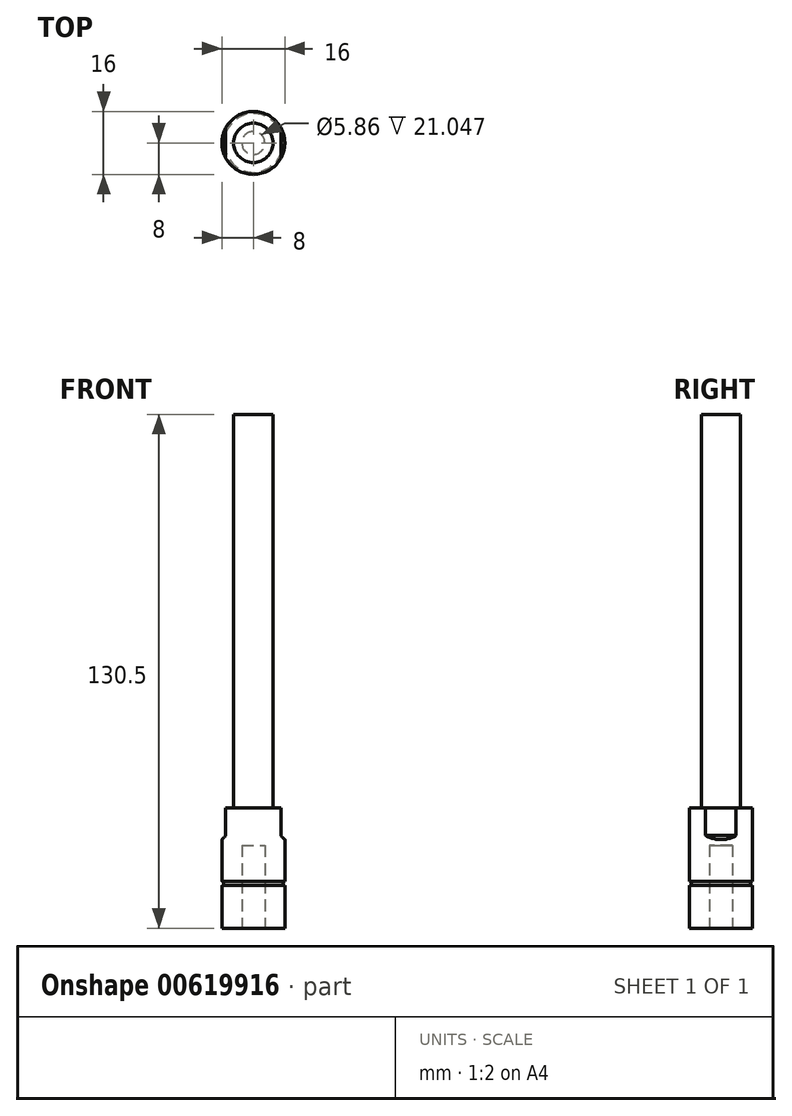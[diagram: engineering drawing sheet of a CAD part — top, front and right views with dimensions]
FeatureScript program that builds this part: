
annotation { "Feature Type Name" : "Feature", "Feature Type Description" : "" }
export const myFeature = defineFeature(function(context is Context, id is Id, definition is map)
    precondition{}
    {
        {
            var Q0;
            Q0=qCreatedBy(makeId("Front.planeOp"),FACE);
            var sketch = newSketch(context, id + "F0", { "sketchPlane" : qUnion([Q0])});
            skLineSegment(sketch, "E0.bottom", {"start": v(2.93, 0) * mm, "end": v(8, 0) * mm});
            skLineSegment(sketch, "E0.top", {"start": v(5, 30.5) * mm, "end": v(8, 30.5) * mm});
            skLineSegment(sketch, "E0.left", {"start": v(0, 21.05) * mm, "end": v(0, 30.5) * mm});
            skLineSegment(sketch, "E0.right", {"start": v(8, 0) * mm, "end": v(8, 10.84) * mm});
            skLineSegment(sketch, "E1.top", {"start": v(0, 130.5) * mm, "end": v(5, 130.5) * mm});
            skLineSegment(sketch, "E1.left", {"start": v(0, 30.5) * mm, "end": v(0, 130.5) * mm});
            skLineSegment(sketch, "E1.right", {"start": v(5, 30.5) * mm, "end": v(5, 130.5) * mm});
            skArc(sketch, "E2", {"start": v(8, 11.84) * mm, "mid": v(7.5, 11.34) * mm, "end": v(8, 10.84) * mm});
            skLineSegment(sketch, "E3.top", {"start": v(0, 21.05) * mm, "end": v(2.93, 21.05) * mm});
            skLineSegment(sketch, "E3.right", {"start": v(2.93, 0) * mm, "end": v(2.93, 21.05) * mm});
            skLineSegment(sketch, "E4.trimOffspring", {"start": v(8, 11.84) * mm, "end": v(8, 30.5) * mm});
            skSolve(sketch);
        }
        {
            var Q0;
            Q0=qSketchRegion(id+"F0",true);
            var Q1;
            Q1=sQuery(id+"F0.wireOp",EDGE,"E1.left");
            revolve(context, id + "F1", {"entities" : qUnion([Q0]), "axis" : qUnion([Q1]), "revolveType" : RevolveType.FULL});
        }
        {
            var Q0;
            Q0=makeQuery(id+"F1.opRevolve","SWEPT_FACE",FACE,{"disambiguationData":[OSD([sQuery(id+"F0.wireOp",EDGE,"E0.top")])]});
            var sketch = newSketch(context, id + "F2", { "sketchPlane" : qUnion([Q0])});
            skLineSegment(sketch, "E5.bottom", {"start": v(7, -15) * mm, "end": v(-7, -15) * mm});
            skLineSegment(sketch, "E5.top", {"start": v(7, 15) * mm, "end": v(-7, 15) * mm});
            skLineSegment(sketch, "E5.left", {"start": v(7, -15) * mm, "end": v(7, 15) * mm});
            skLineSegment(sketch, "E5.right", {"start": v(-7, -15) * mm, "end": v(-7, 15) * mm});
            skPoint(sketch, "E5.middle", {"position": v(0, 0) * mm});
            skLineSegment(sketch, "E6.bottom", {"start": v(9.8, -18.57) * mm, "end": v(-9.8, -18.57) * mm});
            skLineSegment(sketch, "E6.top", {"start": v(9.8, 18.57) * mm, "end": v(-9.8, 18.57) * mm});
            skLineSegment(sketch, "E6.left", {"start": v(9.8, -18.57) * mm, "end": v(9.8, 18.57) * mm});
            skLineSegment(sketch, "E6.right", {"start": v(-9.8, -18.57) * mm, "end": v(-9.8, 18.57) * mm});
            skSolve(sketch);
        }
        {
            var Q0;
            Q0=qSketchRegion(id+"F2",true);
            extrude(context, id + "F3", {"entities" : qUnion([Q0]), "operationType" : NewBodyOperationType.REMOVE, "oppositeDirection" : true, "depth" : 8 * mm, "offsetDistance" : 25 * mm});
        }
        {
            var Q0;
            Q0=makeQuery(id+"F3.boolean.opBoolean","COPY",EDGE,{"derivedFrom":makeQuery(id+"F3.opExtrude","CAP_EDGE",EDGE,{"disambiguationData":[OSD([sQuery(id+"F2.wireOp",EDGE,"E5.right")])],"isStart":false})});
            var Q1;
            Q1=makeQuery(id+"F3.boolean.opBoolean","COPY",EDGE,{"derivedFrom":makeQuery(id+"F3.opExtrude","CAP_EDGE",EDGE,{"disambiguationData":[OSD([sQuery(id+"F2.wireOp",EDGE,"E5.left")])],"isStart":false})});
            chamfer(context, id + "F4", {"entities" : qUnion([Q0, Q1]), "width" : 1 * mm, "tangentPropagation" : true});
        }
    });
